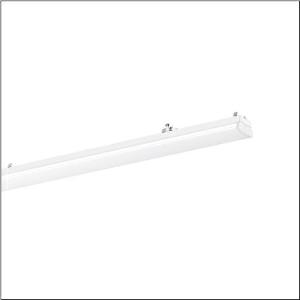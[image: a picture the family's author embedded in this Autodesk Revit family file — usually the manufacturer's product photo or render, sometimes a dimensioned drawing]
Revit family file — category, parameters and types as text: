
# Revit family: licross_r__11_recessed_opal_mo_51tl1ddn495g_fb0a
name_source: partatom
category: Lighting Fixtures
units: mm (PartAtom-declared; Revit-internal decimal feet)

## family parameters
Cut with Voids When Loaded = No
Host = Face
Light Source = No
Part Type = Normal
Room Calculation Point = No
Round Connector Dimension = Use Diameter
Shared = No

## types (1)
- --- (1 x LED, 9710 lm, 56.7 W, 4000K)
    Apparent Load = 57 VA
    CIE Flux Codes = 44 73 91 87 100
    Color Rendering = 80
    Color Temperature = 4000K
    Default Elevation = 1800 mm
    Description = Licross® 11 recessed opal MO, luminaire insert, of sheet steel, coil coated, white, length: 1.500mm, width: 76mm, height: 87mm, LED rated luminous flux: 9.710lm, light colour: 840, control gear: DALI 2, with plug, 5-pole, with phase selection, mains connection: 220..240V, AC, 50/60Hz, rated input power: 57W, halogen-free wiring, primary optical cover: cover, of PMMA, light emission: direct with ceiling illumination distribution, primary light characteristic: symmetric, protection rating (complete): IP40, insulation class (complete): insulation class I (protective earthing), certification: CE, ENEC, VDE, UKCA, protection symbol: D if used in an environment without relevant dust loads with corresponding accessories, impact resistance: IK06, permissible ambient temperature for indoor applications: -25..+35°C, corresponds to IFS (International Featured Standards) requirements for safety and quality in the food industry, reducing of maximum allowable ambient temperature of 5°C with ceiling mounting, LABS conformity tested according to VDMA 24364:2018-05, packaging unit: 1 piece
    Height = 83 mm
    Lamp = 1 x LED
    Lamp Light Flux = 9710 lm
    Lamp Power = 56.7 W
    Lamp count = 1
    Length = 1500 mm
    Luminous efficacy = 171 lm/W
    Manufacturer = Siteco
    ModVariant = No
    Model = 51TL1DDN495G
    Mounting Place = Ceiling
    Mounting Type = Pendant
    Number of Poles = 1
    OnlyDefault = Yes
    Power Factor = 1
    Product Name = Licross® 11 recessed opal MO
    Product group = luminaire insert
    ProductGroupID = 901
    Protection Class = Protection class I
    Protection Degree = IP 40
    RLX_Detail_Level = 1
    RLX_Emergency_Light_Flux = 0 lm
    RLX_Emergency_Type = 0
    RLX_Emergency_Type_DB = No
    RlxData = <blob elided: 27021 chars, md5=87be58dd>
    Socket = socket
    Standby Power = 0 W
    System Light Flux = 9710 lm
    System Power = 57 W
    Type Comments = factory setting: luminous flux: 100 % | dim-lin: 254 | 378 mA
    Type Image = l_1313666.jpg
    URL = http://relux.com
    VarID = @adj_045127
    Voltage = 0 V
    Weight = 0.00 kg
    Width = 76 mm

## geometry (parser evidence)
native form markers: Blend x4, Sweep x12
no freeform markers — native parametric forms only
